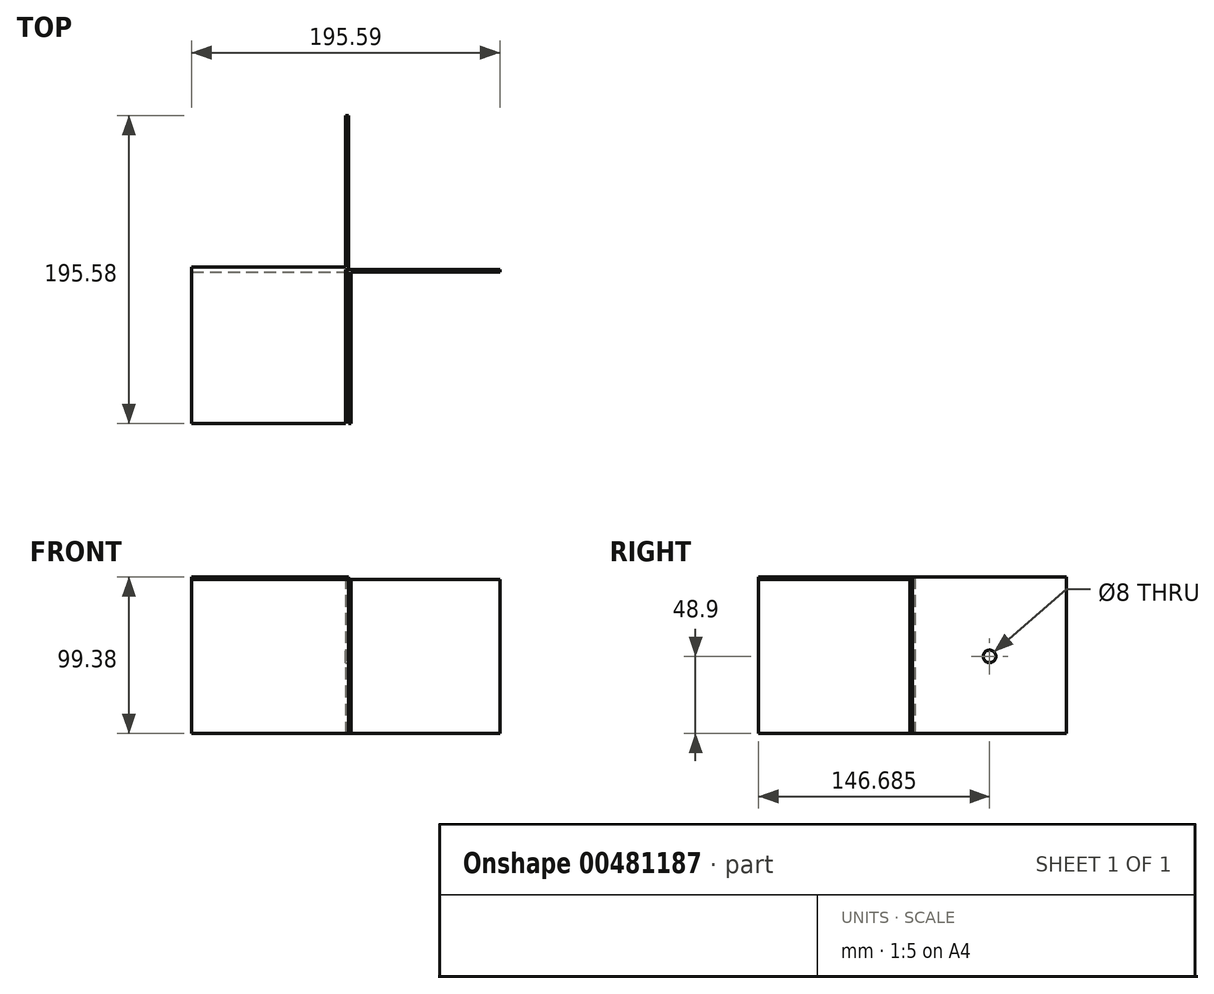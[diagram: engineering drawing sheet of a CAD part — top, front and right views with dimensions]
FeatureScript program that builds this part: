
annotation { "Feature Type Name" : "Feature", "Feature Type Description" : "" }
export const myFeature = defineFeature(function(context is Context, id is Id, definition is map)
    precondition{}
    {
        {
            var Q0;
            Q0=qCreatedBy(makeId("Front.planeOp"),FACE);
            var sketch = newSketch(context, id + "F0", { "sketchPlane" : qUnion([Q0])});
            skLineSegment(sketch, "E0.bottom", {"start": v(-48.9, 48.9) * mm, "end": v(48.9, 48.9) * mm});
            skLineSegment(sketch, "E0.top", {"start": v(-48.9, -48.9) * mm, "end": v(48.9, -48.9) * mm});
            skLineSegment(sketch, "E0.left", {"start": v(-48.9, 48.9) * mm, "end": v(-48.9, -48.9) * mm});
            skLineSegment(sketch, "E0.right", {"start": v(48.9, 48.9) * mm, "end": v(48.9, -48.9) * mm});
            skPoint(sketch, "E1", {"position": v(0, 48.9) * mm});
            skPoint(sketch, "E2", {"position": v(-48.9, 0) * mm});
            skPoint(sketch, "E3", {"position": v(0, 0) * mm});
            skSolve(sketch);
        }
        {
            var Q0;
            Q0=makeQuery(id+"F0.imprint","IMPRINT",FACE,{"disambiguationData":[TD([[makeQuery(id+"F0.imprint","IMPRINT",EDGE,{"derivedFrom":sQuery(id+"F0.wireOp",EDGE,"E0.bottom")}),-1.0]])]});
            extrude(context, id + "F1", {"entities" : qUnion([Q0]), "depth" : 1.59 * mm});
        }
        {
            var Q0;
            Q0=makeQuery(id+"F1.opExtrude","SWEPT_FACE",FACE,{"disambiguationData":[OSD([sQuery(id+"F0.wireOp",EDGE,"E0.bottom")])]});
            var sketch = newSketch(context, id + "F2", { "sketchPlane" : qUnion([Q0])});
            skLineSegment(sketch, "E4.bottom", {"start": v(-48.9, 0) * mm, "end": v(48.9, 0) * mm});
            skLineSegment(sketch, "E4.top", {"start": v(-48.9, -97.8) * mm, "end": v(48.9, -97.8) * mm});
            skLineSegment(sketch, "E4.left", {"start": v(-48.9, 0) * mm, "end": v(-48.9, -97.8) * mm});
            skLineSegment(sketch, "E4.right", {"start": v(48.9, 0) * mm, "end": v(48.9, -97.8) * mm});
            skSolve(sketch);
        }
        {
            var Q0;
            {var subQ0=sQuery(id+"F2.wireOp",EDGE,"E4.top");Q0=makeQuery(id+"F2.imprint","IMPRINT",FACE,{"disambiguationData":[TD([[makeQuery(id+"F2.imprint","IMPRINT",EDGE,{"derivedFrom":subQ0}),1.0]])]});}
            var Q1;
            {var subQ0=sQuery(id+"F2.wireOp",EDGE,"E4.bottom");Q1=makeQuery(id+"F2.imprint","IMPRINT",FACE,{"disambiguationData":[TD([[makeQuery(id+"F2.imprint","IMPRINT",EDGE,{"derivedFrom":subQ0}),-1.0]])]});}
            extrude(context, id + "F3", {"entities" : qUnion([Q0, Q1]), "operationType" : NewBodyOperationType.ADD, "depth" : 1.59 * mm});
        }
        {
            var Q0;
            Q0=makeQuery(id+"F3.boolean.opBoolean","MERGE",FACE,{"derivedFrom":[makeQuery(id+"F1.opExtrude","CAP_FACE",FACE,{"disambiguationData":[OSD([sQuery(id+"F0.wireOp",EDGE,"E0.bottom"),sQuery(id+"F0.wireOp",EDGE,"E0.top"),sQuery(id+"F0.wireOp",EDGE,"E0.left"),sQuery(id+"F0.wireOp",EDGE,"E0.right")])],"isStart":true}),makeQuery(id+"F3.opExtrude","SWEPT_FACE",FACE,{"disambiguationData":[OSD([sQuery(id+"F2.wireOp",EDGE,"E4.bottom")])]})]});
            var sketch = newSketch(context, id + "F4", { "sketchPlane" : qUnion([Q0])});
            skLineSegment(sketch, "E5.bottom", {"start": v(-48.9, 50.48) * mm, "end": v(48.9, 50.48) * mm});
            skLineSegment(sketch, "E5.top", {"start": v(-48.9, -48.9) * mm, "end": v(48.9, -48.9) * mm});
            skLineSegment(sketch, "E5.left", {"start": v(-48.9, 50.48) * mm, "end": v(-48.9, -48.9) * mm});
            skLineSegment(sketch, "E5.right", {"start": v(48.9, 50.48) * mm, "end": v(48.9, -48.9) * mm});
            skSolve(sketch);
        }
        {
            var Q0;
            Q0=makeQuery(id+"F4.imprint","IMPRINT",FACE,{"disambiguationData":[TD([[makeQuery(id+"F4.imprint","IMPRINT",EDGE,{"derivedFrom":sQuery(id+"F4.wireOp",EDGE,"E5.bottom")}),1.0]])]});
            extrude(context, id + "F5", {"entities" : qUnion([Q0]), "operationType" : NewBodyOperationType.ADD, "depth" : 1.59 * mm});
        }
        {
            var Q0;
            Q0=makeQuery(id+"F5.boolean.opBoolean","MERGE",FACE,{"derivedFrom":[makeQuery(id+"F3.boolean.opBoolean","MERGE",FACE,{"derivedFrom":[makeQuery(id+"F1.opExtrude","SWEPT_FACE",FACE,{"disambiguationData":[OSD([sQuery(id+"F0.wireOp",EDGE,"E0.right")])]}),makeQuery(id+"F3.opExtrude","SWEPT_FACE",FACE,{"disambiguationData":[OSD([sQuery(id+"F2.wireOp",EDGE,"E4.right")])]})]}),makeQuery(id+"F5.opExtrude","SWEPT_FACE",FACE,{"disambiguationData":[OSD([sQuery(id+"F4.wireOp",EDGE,"E5.left")])]})]});
            var sketch = newSketch(context, id + "F6", { "sketchPlane" : qUnion([Q0])});
            skLineSegment(sketch, "E6.bottom", {"start": v(0, -48.9) * mm, "end": v(97.8, -48.9) * mm});
            skLineSegment(sketch, "E6.top", {"start": v(0, 50.48) * mm, "end": v(97.79, 50.48) * mm});
            skLineSegment(sketch, "E6.left", {"start": v(0, -48.9) * mm, "end": v(0, 50.48) * mm});
            skLineSegment(sketch, "E6.right", {"start": v(97.8, -48.9) * mm, "end": v(97.79, 50.48) * mm});
            skSolve(sketch);
        }
        {
            var Q0;
            {var subQ2=sQuery(id+"F6.wireOp",EDGE,"E6.right");Q0=makeQuery(id+"F6.imprint","IMPRINT",FACE,{"disambiguationData":[TD([[makeQuery(id+"F6.imprint","IMPRINT",EDGE,{"derivedFrom":subQ2}),1.0]])]});}
            var Q1;
            {var subQ3=sQuery(id+"F6.wireOp",EDGE,"E6.left");Q1=makeQuery(id+"F6.imprint","IMPRINT",FACE,{"disambiguationData":[TD([[makeQuery(id+"F6.imprint","IMPRINT",EDGE,{"derivedFrom":subQ3}),-1.0]])]});}
            extrude(context, id + "F7", {"entities" : qUnion([Q0, Q1]), "operationType" : NewBodyOperationType.ADD, "depth" : 1.59 * mm});
        }
        {
            var Q0;
            Q0=makeQuery(id+"F7.opExtrude","CAP_FACE",FACE,{"disambiguationData":[OSD([sQuery(id+"F6.wireOp",EDGE,"E6.bottom"),sQuery(id+"F6.wireOp",EDGE,"E6.top"),sQuery(id+"F6.wireOp",EDGE,"E6.left"),sQuery(id+"F6.wireOp",EDGE,"E6.right")])],"isStart":false});
            var sketch = newSketch(context, id + "F8", { "sketchPlane" : qUnion([Q0])});
            skCircle(sketch, "E7", {"center": v(48.9, 0) * mm, "radius": 4 * mm});
            skPoint(sketch, "E7.centerSnap0", {"position": v(48.9, 50.48) * mm});
            skSolve(sketch);
        }
        {
            var Q0;
            Q0=makeQuery(id+"F8.imprint","IMPRINT",FACE,{"disambiguationData":[TD([[makeQuery(id+"F8.imprint","IMPRINT",EDGE,{"derivedFrom":sQuery(id+"F8.wireOp",EDGE,"E7")}),1.0]])]});
            extrude(context, id + "F9", {"entities" : qUnion([Q0]), "operationType" : NewBodyOperationType.REMOVE, "oppositeDirection" : true, "depth" : 25.4 * mm});
        }
        {
            var Q0;
            Q0=makeQuery(id+"F7.opExtrude","SWEPT_FACE",FACE,{"disambiguationData":[OSD([sQuery(id+"F6.wireOp",EDGE,"E6.left")])]});
            var sketch = newSketch(context, id + "F10", { "sketchPlane" : qUnion([Q0])});
            skLineSegment(sketch, "E8.bottom", {"start": v(48.9, 48.9) * mm, "end": v(146.69, 48.9) * mm});
            skLineSegment(sketch, "E8.top", {"start": v(48.9, -48.9) * mm, "end": v(146.69, -48.9) * mm});
            skLineSegment(sketch, "E8.left", {"start": v(48.9, 48.9) * mm, "end": v(48.9, -48.9) * mm});
            skLineSegment(sketch, "E8.right", {"start": v(146.69, 48.9) * mm, "end": v(146.69, -48.9) * mm});
            skSolve(sketch);
        }
        {
            var Q0;
            {var subQ0=sQuery(id+"F10.wireOp",EDGE,"E8.right");Q0=makeQuery(id+"F10.imprint","IMPRINT",FACE,{"disambiguationData":[TD([[makeQuery(id+"F10.imprint","IMPRINT",EDGE,{"derivedFrom":subQ0}),-1.0]])]});}
            var Q1;
            {var subQ0=sQuery(id+"F10.wireOp",EDGE,"E8.left");Q1=makeQuery(id+"F10.imprint","IMPRINT",FACE,{"disambiguationData":[TD([[makeQuery(id+"F10.imprint","IMPRINT",EDGE,{"derivedFrom":subQ0}),-1.0]])]});}
            extrude(context, id + "F11", {"entities" : qUnion([Q0, Q1]), "operationType" : NewBodyOperationType.ADD, "depth" : 1.59 * mm});
        }
        {
            var Q0;
            Q0=makeQuery(id+"F7.opExtrude","CAP_FACE",FACE,{"disambiguationData":[OSD([sQuery(id+"F6.wireOp",EDGE,"E6.bottom"),sQuery(id+"F6.wireOp",EDGE,"E6.top"),sQuery(id+"F6.wireOp",EDGE,"E6.left"),sQuery(id+"F6.wireOp",EDGE,"E6.right")])],"isStart":false});
            var sketch = newSketch(context, id + "F12", { "sketchPlane" : qUnion([Q0])});
            skLineSegment(sketch, "E9.bottom", {"start": v(0, 48.9) * mm, "end": v(-97.8, 48.9) * mm});
            skLineSegment(sketch, "E9.top", {"start": v(0, -48.9) * mm, "end": v(-97.79, -48.9) * mm});
            skLineSegment(sketch, "E9.left", {"start": v(0, 48.9) * mm, "end": v(0, -48.9) * mm});
            skLineSegment(sketch, "E9.right", {"start": v(-97.8, 48.9) * mm, "end": v(-97.8, -48.9) * mm});
            skSolve(sketch);
        }
        {
            var Q0;
            Q0 = qSketchRegion(id + "F12", true);
            extrude(context, id + "F13", {"entities" : qUnion([Q0]), "operationType" : NewBodyOperationType.ADD, "depth" : 1.59 * mm});
        }
    });
